# Revit family: Ребристая плита перекрытия из сборного железобетона(ГОСТ 27215-87)
name_source: partatom
category: Каркас несущий
revit_build: Autodesk Revit Structure 2016 (Build: 20150220_1215(x64)
units: mm (PartAtom-declared; Revit-internal decimal feet)

## family parameters
Всегда вертикально = Нет
Всегда экспортировать в виде геометрии = Нет
Материал для поведения модели = Прочее
На основе рабочей плоскости = Да
Общий = Да
Округление длины несущего каркаса = 0 мм
Показывать семейство разрезанным на планах = Да
При загрузке вырезать с полостями = Нет
Условное обозначение = Из семейства
Форма сечения = Не задано

## types (4) — shared parameters
R = 50 мм
b1 = 85 мм
b2 = 35 мм
b4 = 100 мм
b5 = 45 мм
b6 = 20 мм
h = 400 мм
hf = 50 мм
ВысотаРебра = 200 мм
Длина1 = 1350 мм
Код по классификатору = B10
Материал несущих конструкций = Бетон - Сборный железобетон - 35 МПa
Отметка по умолчанию = 1219 мм
Ребро1_ДлинаСверху = 100 мм
Ребро1_ДлинаСнизу = 50 мм

## per-type parameters (varying)
| type | b |
| 1P3 | 1485 мм |
| 1P4 | 1485 мм |
| 1P5 | 935 мм |
| 1P6 | 935 мм |

## geometry (parser evidence)
native form markers: Blend x4
no freeform markers — native parametric forms only
